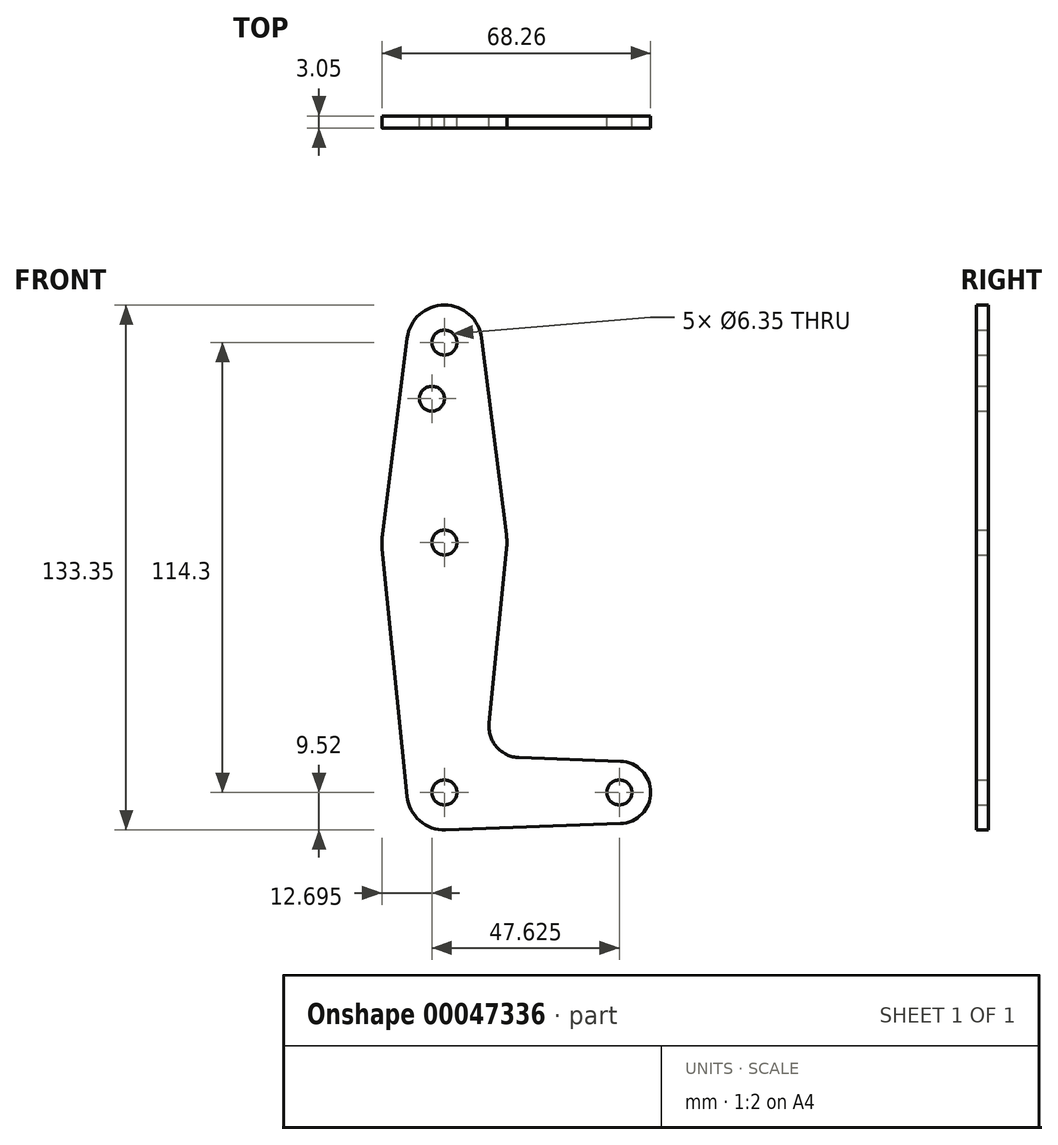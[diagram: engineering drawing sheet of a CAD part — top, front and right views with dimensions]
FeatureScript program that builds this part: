
annotation { "Feature Type Name" : "Feature", "Feature Type Description" : "" }
export const myFeature = defineFeature(function(context is Context, id is Id, definition is map)
    precondition{}
    {
        {
            var Q0;
            Q0=qCreatedBy(makeId("Front.planeOp"),FACE);
            var sketch = newSketch(context, id + "F0", { "sketchPlane" : qUnion([Q0])});
            skLineSegment(sketch, "E0", {"start": v(0, 114.3) * mm, "end": v(0, 0) * mm, "construction": true});
            skLineSegment(sketch, "E1", {"start": v(0, 0) * mm, "end": v(44.45, 0) * mm, "construction": true});
            skCircle(sketch, "E2", {"center": v(0, 114.3) * mm, "radius": 9.53 * mm});
            skCircle(sketch, "E3", {"center": v(0, 63.5) * mm, "radius": 15.88 * mm});
            skCircle(sketch, "E4", {"center": v(0, 0) * mm, "radius": 9.53 * mm});
            skCircle(sketch, "E5", {"center": v(44.45, 0) * mm, "radius": 7.94 * mm});
            skLineSegment(sketch, "E6", {"start": v(9.45, 115.5) * mm, "end": v(15.75, 65.48) * mm});
            skLineSegment(sketch, "E7.MirrorCS", {"start": v(-9.45, 115.5) * mm, "end": v(-15.75, 65.48) * mm});
            skLineSegment(sketch, "E8", {"start": v(15.8, 61.91) * mm, "end": v(11.34, 17.6) * mm});
            skLineSegment(sketch, "E9.MirrorCS", {"start": v(-15.8, 61.91) * mm, "end": v(-9.48, -0.95) * mm});
            skLineSegment(sketch, "E10", {"start": v(18.97, 8.85) * mm, "end": v(44.73, 7.93) * mm});
            skLineSegment(sketch, "E11.MirrorCS", {"start": v(0.34, -9.52) * mm, "end": v(44.73, -7.93) * mm});
            skCircle(sketch, "E12", {"center": v(0, 114.3) * mm, "radius": 3.18 * mm});
            skCircle(sketch, "E13", {"center": v(-3.17, 100.03) * mm, "radius": 3.18 * mm});
            skCircle(sketch, "E14", {"center": v(0, 63.5) * mm, "radius": 3.18 * mm});
            skCircle(sketch, "E15", {"center": v(0, 0) * mm, "radius": 3.18 * mm});
            skCircle(sketch, "E16", {"center": v(44.45, 0) * mm, "radius": 3.18 * mm});
            skPoint(sketch, "E17.newPointA", {"position": v(9.48, -0.95) * mm});
            skPoint(sketch, "E17.newPointB", {"position": v(0.34, 9.52) * mm});
            skArc(sketch, "E17.filletArc", {"start": v(11.34, 17.6) * mm, "mid": v(13.26, 11.57) * mm, "end": v(18.97, 8.85) * mm});
            skSolve(sketch);
        }
        {
            var Q0;
            Q0=makeQuery(id+"F0.imprint","IMPRINT",FACE,{"disambiguationData":[TD([[makeQuery(id+"F0.imprint","IMPRINT",EDGE,{"derivedFrom":sQuery(id+"F0.wireOp",EDGE,"E12")}),-1.0]])]});
            var Q1;
            Q1=makeQuery(id+"F0.imprint","IMPRINT",FACE,{"disambiguationData":[TD([[makeQuery(id+"F0.imprint","IMPRINT",EDGE,{"derivedFrom":sQuery(id+"F0.wireOp",EDGE,"E15")}),-1.0]])]});
            var Q2;
            Q2=makeQuery(id+"F0.imprint","IMPRINT",FACE,{"disambiguationData":[TD([[makeQuery(id+"F0.imprint","IMPRINT",EDGE,{"derivedFrom":sQuery(id+"F0.wireOp",EDGE,"E16")}),-1.0]])]});
            var Q3;
            {var subQ2=sQuery(id+"F0.wireOp",EDGE,"E6");Q3=makeQuery(id+"F0.imprint","IMPRINT",FACE,{"disambiguationData":[TD([[makeQuery(id+"F0.imprint","IMPRINT",EDGE,{"derivedFrom":subQ2}),-1.0]])]});}
            var Q4;
            Q4=makeQuery(id+"F0.imprint","IMPRINT",FACE,{"disambiguationData":[TD([[makeQuery(id+"F0.imprint","IMPRINT",EDGE,{"derivedFrom":sQuery(id+"F0.wireOp",EDGE,"E14")}),-1.0]])]});
            var Q5;
            {var subQ3=sQuery(id+"F0.wireOp",EDGE,"E8");Q5=makeQuery(id+"F0.imprint","IMPRINT",FACE,{"disambiguationData":[TD([[makeQuery(id+"F0.imprint","IMPRINT",EDGE,{"derivedFrom":subQ3}),-1.0]])]});}
            extrude(context, id + "F1", {"entities" : qUnion([Q0, Q1, Q2, Q3, Q4, Q5]), "depth" : 3.05 * mm});
        }
    });
